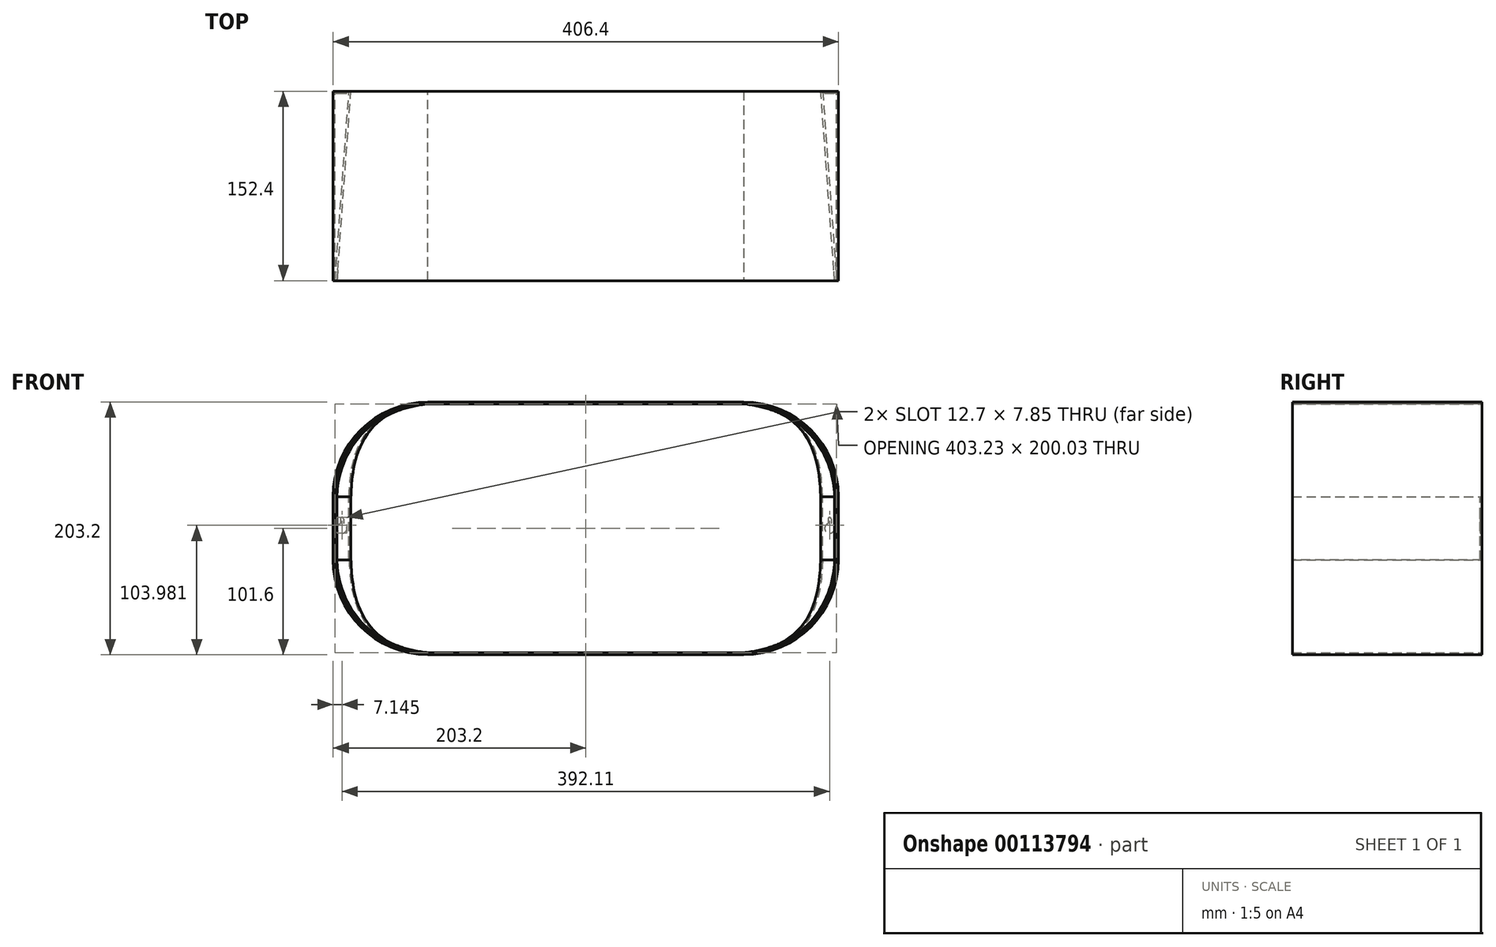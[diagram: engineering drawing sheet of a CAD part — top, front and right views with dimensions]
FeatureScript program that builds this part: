
annotation { "Feature Type Name" : "Feature", "Feature Type Description" : "" }
export const myFeature = defineFeature(function(context is Context, id is Id, definition is map)
    precondition{}
    {
        {
            var Q0;
            Q0=qCreatedBy(makeId("Front.planeOp"),FACE);
            var sketch = newSketch(context, id + "F0", { "sketchPlane" : qUnion([Q0])});
            skLineSegment(sketch, "E0.bottom", {"start": v(127, -101.6) * mm, "end": v(-127, -101.6) * mm});
            skLineSegment(sketch, "E0.top", {"start": v(127, 101.6) * mm, "end": v(-127, 101.6) * mm});
            skLineSegment(sketch, "E0.left", {"start": v(203.2, -25.4) * mm, "end": v(203.2, 25.4) * mm});
            skLineSegment(sketch, "E0.right", {"start": v(-203.2, -25.4) * mm, "end": v(-203.2, 25.4) * mm});
            skPoint(sketch, "E0.middle", {"position": v(0, 0) * mm});
            skPoint(sketch, "E1.visualSharp", {"position": v(-203.2, 101.6) * mm});
            skArc(sketch, "E1.filletArc", {"start": v(-127, 101.6) * mm, "mid": v(-180.88, 79.28) * mm, "end": v(-203.2, 25.4) * mm});
            skPoint(sketch, "E2.visualSharp", {"position": v(203.2, 101.6) * mm});
            skArc(sketch, "E2.filletArc", {"start": v(203.2, 25.4) * mm, "mid": v(180.88, 79.28) * mm, "end": v(127, 101.6) * mm});
            skPoint(sketch, "E3.visualSharp", {"position": v(-203.2, -101.6) * mm});
            skArc(sketch, "E3.filletArc", {"start": v(-203.2, -25.4) * mm, "mid": v(-180.88, -79.28) * mm, "end": v(-127, -101.6) * mm});
            skPoint(sketch, "E4.visualSharp", {"position": v(203.2, -101.6) * mm});
            skArc(sketch, "E4.filletArc", {"start": v(127, -101.6) * mm, "mid": v(180.88, -79.28) * mm, "end": v(203.2, -25.4) * mm});
            skArc(sketch, "E5.0", {"start": v(201.62, 25.4) * mm, "mid": v(179.76, 78.16) * mm, "end": v(127, 100.02) * mm});
            skLineSegment(sketch, "E5.1", {"start": v(201.62, -25.4) * mm, "end": v(201.62, 25.4) * mm});
            skLineSegment(sketch, "E5.2", {"start": v(127, 100.02) * mm, "end": v(-127, 100.02) * mm});
            skArc(sketch, "E5.3", {"start": v(127, -100.02) * mm, "mid": v(179.76, -78.16) * mm, "end": v(201.62, -25.4) * mm});
            skArc(sketch, "E5.4", {"start": v(-127, 100.02) * mm, "mid": v(-179.76, 78.16) * mm, "end": v(-201.62, 25.4) * mm});
            skLineSegment(sketch, "E5.5", {"start": v(-201.62, -25.4) * mm, "end": v(-201.62, 25.4) * mm});
            skArc(sketch, "E5.6", {"start": v(-201.62, -25.4) * mm, "mid": v(-179.76, -78.16) * mm, "end": v(-127, -100.02) * mm});
            skLineSegment(sketch, "E5.7", {"start": v(127, -100.02) * mm, "end": v(-127, -100.02) * mm});
            skSolve(sketch);
        }
        {
            var Q0;
            Q0=makeQuery(id+"F0.imprint","IMPRINT",FACE,{"disambiguationData":[TD([[makeQuery(id+"F0.imprint","IMPRINT",EDGE,{"derivedFrom":sQuery(id+"F0.wireOp",EDGE,"E0.bottom")}),-1.0]])]});
            extrude(context, id + "F1", {"entities" : qUnion([Q0]), "depth" : 152.4 * mm});
        }
        {
            var Q0;
            Q0=makeQuery(id+"F1.opExtrude","CAP_FACE",FACE,{"disambiguationData":[OSD([sQuery(id+"F0.wireOp",EDGE,"E0.bottom"),sQuery(id+"F0.wireOp",EDGE,"E0.top"),sQuery(id+"F0.wireOp",EDGE,"E0.left"),sQuery(id+"F0.wireOp",EDGE,"E0.right"),sQuery(id+"F0.wireOp",EDGE,"E1.filletArc"),sQuery(id+"F0.wireOp",EDGE,"E2.filletArc"),sQuery(id+"F0.wireOp",EDGE,"E3.filletArc"),sQuery(id+"F0.wireOp",EDGE,"E4.filletArc"),sQuery(id+"F0.wireOp",EDGE,"E5.0"),sQuery(id+"F0.wireOp",EDGE,"E5.1"),sQuery(id+"F0.wireOp",EDGE,"E5.2"),sQuery(id+"F0.wireOp",EDGE,"E5.3"),sQuery(id+"F0.wireOp",EDGE,"E5.4"),sQuery(id+"F0.wireOp",EDGE,"E5.5"),sQuery(id+"F0.wireOp",EDGE,"E5.6"),sQuery(id+"F0.wireOp",EDGE,"E5.7")])],"isStart":false});
            var sketch = newSketch(context, id + "F2", { "sketchPlane" : qUnion([Q0])});
            skArc(sketch, "E6.0", {"start": v(-127, 100.02) * mm, "mid": v(-179.76, 78.16) * mm, "end": v(-201.62, 25.4) * mm});
            skLineSegment(sketch, "E7.0", {"start": v(-201.62, -25.4) * mm, "end": v(-201.62, 25.4) * mm});
            skArc(sketch, "E8.0", {"start": v(-201.62, -25.4) * mm, "mid": v(-179.76, -78.16) * mm, "end": v(-127, -100.02) * mm});
            skLineSegment(sketch, "E9.1", {"start": v(-200.05, -25.4) * mm, "end": v(-200.05, 25.4) * mm});
            skFitSpline(sketch, "E10", {"points": [v(-200.05, 25.4) * mm, v(-127, 100.02) * mm], "startDerivative": vector(-0.25, 46.6) * mm, "endDerivative": vector(194.49, 21.97) * mm});
            skFitSpline(sketch, "E11.MirrorCS", {"points": [v(-200.05, -25.4) * mm, v(-127, -100.02) * mm], "startDerivative": vector(-0.25, -46.6) * mm, "endDerivative": vector(194.49, -21.97) * mm});
            skSolve(sketch);
        }
        {
            var Q0;
            Q0=makeQuery(id+"F1.opExtrude","CAP_FACE",FACE,{"disambiguationData":[OSD([sQuery(id+"F0.wireOp",EDGE,"E0.bottom"),sQuery(id+"F0.wireOp",EDGE,"E0.top"),sQuery(id+"F0.wireOp",EDGE,"E0.left"),sQuery(id+"F0.wireOp",EDGE,"E0.right"),sQuery(id+"F0.wireOp",EDGE,"E1.filletArc"),sQuery(id+"F0.wireOp",EDGE,"E2.filletArc"),sQuery(id+"F0.wireOp",EDGE,"E3.filletArc"),sQuery(id+"F0.wireOp",EDGE,"E4.filletArc"),sQuery(id+"F0.wireOp",EDGE,"E5.0"),sQuery(id+"F0.wireOp",EDGE,"E5.1"),sQuery(id+"F0.wireOp",EDGE,"E5.2"),sQuery(id+"F0.wireOp",EDGE,"E5.3"),sQuery(id+"F0.wireOp",EDGE,"E5.4"),sQuery(id+"F0.wireOp",EDGE,"E5.5"),sQuery(id+"F0.wireOp",EDGE,"E5.6"),sQuery(id+"F0.wireOp",EDGE,"E5.7")])],"isStart":true});
            var sketch = newSketch(context, id + "F3", { "sketchPlane" : qUnion([Q0])});
            skLineSegment(sketch, "E12.1", {"start": v(188.92, -25.4) * mm, "end": v(188.92, 25.4) * mm});
            skFitSpline(sketch, "E13", {"points": [v(188.92, 25.4) * mm, v(127, 100.02) * mm], "startDerivative": vector(-4.18, 39.18) * mm, "endDerivative": vector(-191.73, 15.1) * mm});
            skFitSpline(sketch, "E14.MirrorCS", {"points": [v(188.92, -25.4) * mm, v(127, -100.02) * mm], "startDerivative": vector(-4.18, -39.18) * mm, "endDerivative": vector(-191.73, -15.1) * mm});
            skLineSegment(sketch, "E15.0", {"start": v(190.5, -25.4) * mm, "end": v(190.5, 25.4) * mm});
            skFitSpline(sketch, "E16", {"points": [v(190.5, 25.4) * mm, v(127, 100.02) * mm], "startDerivative": vector(-4.45, 29.57) * mm, "endDerivative": vector(-200.48, 10.71) * mm});
            skFitSpline(sketch, "E17.MirrorCS", {"points": [v(190.5, -25.4) * mm, v(127, -100.02) * mm], "startDerivative": vector(-4.45, -29.57) * mm, "endDerivative": vector(-200.48, -10.71) * mm});
            skSolve(sketch);
        }
        {
            var Q0;
            Q0 = qSketchRegion(id + "F2", true);
            var Q1;
            Q1 = qSketchRegion(id + "F3", true);
            loft(context, id + "F4", {"sheetProfilesArray" : [{ "sheetProfileEntities" : qUnion([Q0]) }, { "sheetProfileEntities" : qUnion([Q1]) }]});
        }
        {
            var Q0;
            Q0=makeQuery(id+"F1.opExtrude","CAP_EDGE",EDGE,{"disambiguationData":[OSD([sQuery(id+"F0.wireOp",EDGE,"E5.5")])],"isStart":true});
            var Q1;
            Q1=sQuery(id+"F3.wireOp",EDGE,"E15.0");
            cPlane(context, id + "F5", {"entities" : qUnion([Q0, Q1]), "cplaneType" : CPlaneType.LINE_ANGLE, "offset" : 25.4 * mm, "angle" : 0 * degree, "width" : 152.4 * mm, "height" : 152.4 * mm});
        }
        {
            var Q0;
            Q0=qCreatedBy(id+"F5.planeOp",FACE);
            var sketch = newSketch(context, id + "F6", { "sketchPlane" : qUnion([Q0])});
            skLineSegment(sketch, "E18.0", {"start": v(190.5, -25.4) * mm, "end": v(190.5, 25.4) * mm});
            skLineSegment(sketch, "E19.0", {"start": v(201.62, -25.4) * mm, "end": v(201.62, 25.4) * mm});
            skFitSpline(sketch, "E20.0", {"points": [v(201.62, 25.4) * mm, v(197.9, 25.4) * mm, v(194.2, 25.4) * mm, v(190.5, 25.4) * mm]});
            skFitSpline(sketch, "E21.0", {"points": [v(201.62, -25.4) * mm, v(197.9, -25.4) * mm, v(194.2, -25.4) * mm, v(190.5, -25.4) * mm]});
            skSolve(sketch);
        }
        {
            var Q0;
            Q0 = qSketchRegion(id + "F6", true);
            extrude(context, id + "F7", {"entities" : qUnion([Q0]), "oppositeDirection" : true, "depth" : 1.59 * mm});
        }
        {
            var Q0;
            Q0=makeQuery(id+"F7.opExtrude","CAP_FACE",FACE,{"disambiguationData":[OSD([sQuery(id+"F6.wireOp",EDGE,"E18.0"),sQuery(id+"F6.wireOp",EDGE,"E19.0"),sQuery(id+"F6.wireOp",EDGE,"E20.0"),sQuery(id+"F6.wireOp",EDGE,"E21.0")])],"isStart":true});
            var sketch = newSketch(context, id + "F8", { "sketchPlane" : qUnion([Q0])});
            skLineSegment(sketch, "E22", {"start": v(190.5, 25.4) * mm, "end": v(201.62, 25.4) * mm, "construction": true});
            skArc(sketch, "E23", {"start": v(194.86, 3.79) * mm, "mid": v(196.05, -3.97) * mm, "end": v(197.25, 3.79) * mm});
            skPoint(sketch, "E24.second.point", {"position": v(196.05, 6.35) * mm});
            skPoint(sketch, "E24.third.point", {"position": v(193.67, 6.35) * mm});
            skPoint(sketch, "E24.third.point.positionSnap0", {"position": v(196.05, 6.35) * mm});
            skArc(sketch, "E25", {"start": v(197.25, 7.54) * mm, "mid": v(196.05, 8.73) * mm, "end": v(194.86, 7.54) * mm});
            skLineSegment(sketch, "E26", {"start": v(194.86, 7.54) * mm, "end": v(194.86, 3.79) * mm});
            skLineSegment(sketch, "E27", {"start": v(197.25, 7.54) * mm, "end": v(197.25, 3.79) * mm});
            skPoint(sketch, "E28.orphan", {"position": v(196.05, 3.97) * mm});
            skPoint(sketch, "E29.end.orphan", {"position": v(196.05, 8.73) * mm});
            skSolve(sketch);
        }
        {
            var Q0;
            Q0 = qSketchRegion(id + "F8", true);
            extrude(context, id + "F9", {"entities" : qUnion([Q0]), "operationType" : NewBodyOperationType.REMOVE, "oppositeDirection" : true, "depth" : 1.6 * mm});
        }
        {
            var Q0;
            Q0=makeQuery(id+"F7.opExtrude","SWEPT_BODY",BODY,{"disambiguationData":[OSD([sQuery(id+"F6.wireOp",EDGE,"E18.0"),sQuery(id+"F6.wireOp",EDGE,"E19.0"),sQuery(id+"F6.wireOp",EDGE,"E20.0"),sQuery(id+"F6.wireOp",EDGE,"E21.0")])]});
            var Q1;
            Q1=makeQuery(id+"F4.opLoft","SWEPT_BODY",BODY,{"disambiguationData":[OSD([makeQuery(id+"F2.imprint","IMPRINT",FACE,{"disambiguationData":[TD([[makeQuery(id+"F2.imprint","IMPRINT",EDGE,{"derivedFrom":sQuery(id+"F2.wireOp",EDGE,"E6.0")}),1.0]])]}),makeQuery(id+"F3.imprint","IMPRINT",FACE,{"disambiguationData":[TD([[makeQuery(id+"F3.imprint","IMPRINT",EDGE,{"derivedFrom":sQuery(id+"F3.wireOp",EDGE,"E12.1")}),-1.0]])]})])]});
            var Q2;
            Q2=qCreatedBy(makeId("Right.planeOp"),FACE);
            mirror(context, id + "F10", {"entities" : qUnion([Q0, Q1]), "mirrorPlane" : qUnion([Q2])});
        }
    });
